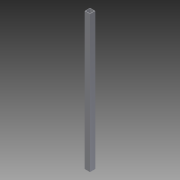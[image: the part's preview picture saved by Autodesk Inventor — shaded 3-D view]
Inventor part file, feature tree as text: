
AUTODESK INVENTOR PART (.ipt)
format: ipt  version: 2013 (Build 170138000, 138)  size: 77,312 bytes
history: native  units: in
note: dims shown in document units (in); Inventor stores cm internally (conversion verified against a paired STEP export)
features: extrude x1, sketch x1
ambient origin geometry x8: Origin, YZ Plane, XZ Plane, XY Plane, X Axis, Y Axis, Z Axis, Center Point
bodies: Solid1 (feature_tree)
feature tree (2):
  extrude  "Extrusion1"  Depth=1.0in
  sketch  "Sketch1"  dims[d0=1.0in d2=1.0in d3=0.0625in d4=26.375in d5=0.0in]
